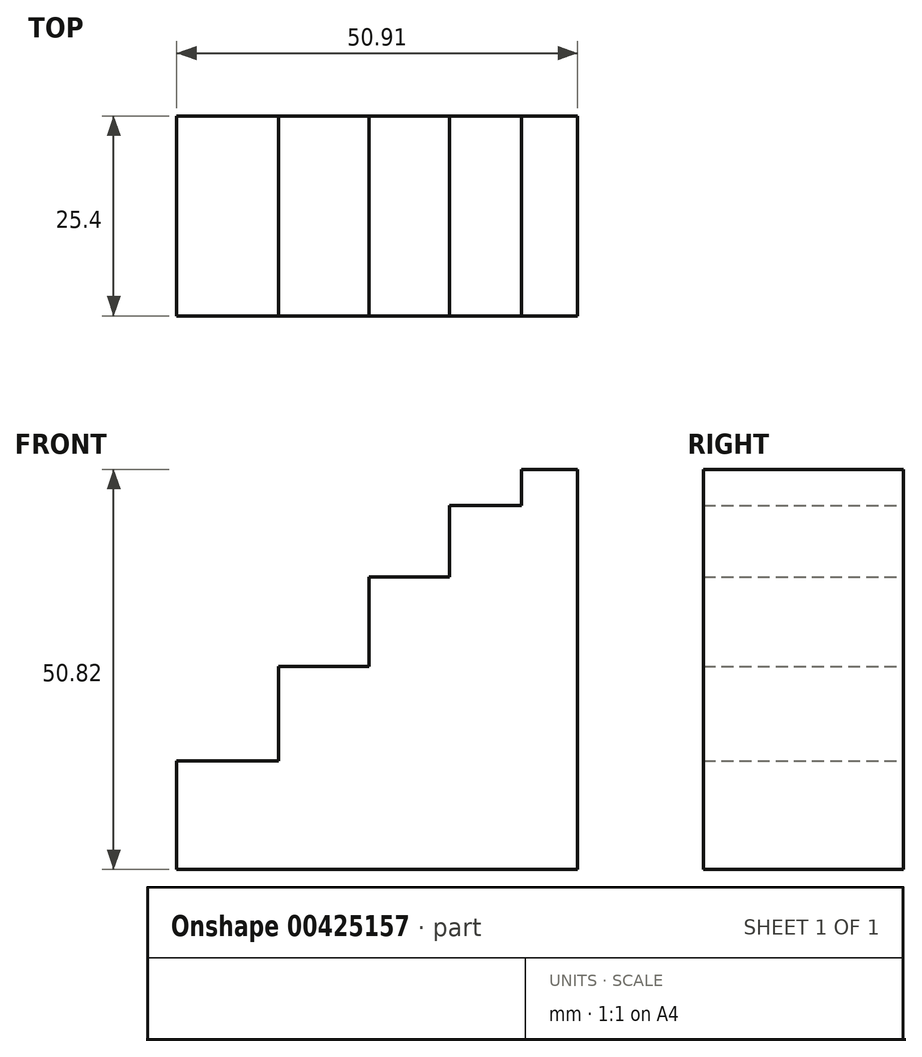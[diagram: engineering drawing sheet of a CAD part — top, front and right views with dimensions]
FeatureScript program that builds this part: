
annotation { "Feature Type Name" : "Feature", "Feature Type Description" : "" }
export const myFeature = defineFeature(function(context is Context, id is Id, definition is map)
    precondition{}
    {
        {
            var Q0;
            Q0=qCreatedBy(makeId("Front.planeOp"),FACE);
            var sketch = newSketch(context, id + "F0", { "sketchPlane" : qUnion([Q0])});
            skLineSegment(sketch, "E0.bottom", {"start": v(0, 0) * mm, "end": v(-50.9, 0) * mm});
            skLineSegment(sketch, "E0.top", {"start": v(0, 50.82) * mm, "end": v(-50.9, 50.82) * mm});
            skLineSegment(sketch, "E0.left", {"start": v(0, 0) * mm, "end": v(0, 50.82) * mm});
            skLineSegment(sketch, "E0.right", {"start": v(-50.9, 0) * mm, "end": v(-50.9, 50.82) * mm});
            skLineSegment(sketch, "E1", {"start": v(-50.9, 13.78) * mm, "end": v(-37.95, 13.78) * mm});
            skLineSegment(sketch, "E2", {"start": v(-37.95, 13.78) * mm, "end": v(-37.95, 25.82) * mm});
            skLineSegment(sketch, "E3", {"start": v(-37.95, 25.82) * mm, "end": v(-26.46, 25.82) * mm});
            skLineSegment(sketch, "E4", {"start": v(-26.46, 25.82) * mm, "end": v(-26.46, 37.13) * mm});
            skLineSegment(sketch, "E5", {"start": v(-26.46, 37.13) * mm, "end": v(-16.24, 37.13) * mm});
            skLineSegment(sketch, "E6", {"start": v(-16.24, 37.13) * mm, "end": v(-16.24, 46.25) * mm});
            skLineSegment(sketch, "E7", {"start": v(-16.24, 46.25) * mm, "end": v(-7.12, 46.25) * mm});
            skLineSegment(sketch, "E8", {"start": v(-7.12, 46.25) * mm, "end": v(-7.12, 50.82) * mm});
            skSolve(sketch);
        }
        {
            var Q0;
            {var subQ1=sQuery(id+"F0.wireOp",EDGE,"E0.bottom");Q0=makeQuery(id+"F0.imprint","IMPRINT",FACE,{"disambiguationData":[TD([[makeQuery(id+"F0.imprint","IMPRINT",EDGE,{"derivedFrom":subQ1}),-1.0]])]});}
            extrude(context, id + "F1", {"entities" : qUnion([Q0]), "depth" : 25.4 * mm});
        }
    });
